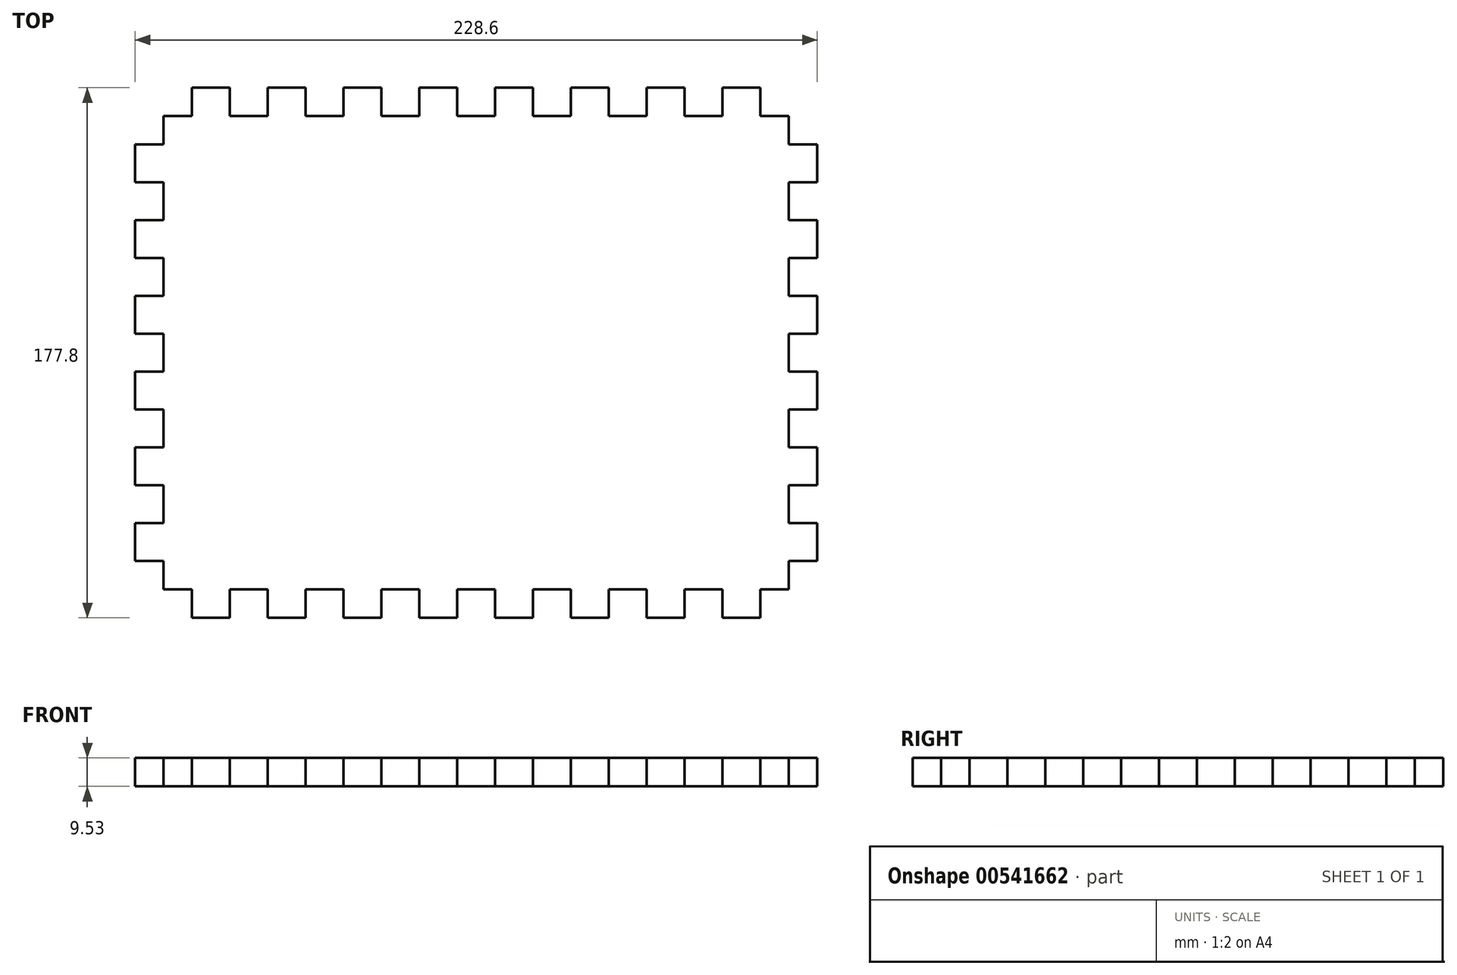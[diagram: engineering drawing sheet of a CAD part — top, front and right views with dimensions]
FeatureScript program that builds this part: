
annotation { "Feature Type Name" : "Feature", "Feature Type Description" : "" }
export const myFeature = defineFeature(function(context is Context, id is Id, definition is map)
    precondition{}
    {
        {
            var Q0;
            Q0=qCreatedBy(makeId("Top.planeOp"),FACE);
            var sketch = newSketch(context, id + "F0", { "sketchPlane" : qUnion([Q0])});
            skLineSegment(sketch, "E0.bottom", {"start": v(19.05, 0) * mm, "end": v(31.75, 0) * mm});
            skLineSegment(sketch, "E0.left", {"start": v(0, -19.05) * mm, "end": v(0, -31.75) * mm});
            skLineSegment(sketch, "E1", {"start": v(9.52, -9.53) * mm, "end": v(19.05, -9.53) * mm});
            skLineSegment(sketch, "E2", {"start": v(19.05, -9.53) * mm, "end": v(19.05, 0) * mm});
            skLineSegment(sketch, "E3", {"start": v(31.75, 0) * mm, "end": v(31.75, -9.53) * mm});
            skLineSegment(sketch, "E4", {"start": v(31.75, -9.53) * mm, "end": v(44.45, -9.53) * mm});
            skLineSegment(sketch, "E5", {"start": v(44.45, -9.53) * mm, "end": v(44.45, 0) * mm});
            skLineSegment(sketch, "E6", {"start": v(44.45, 0) * mm, "end": v(57.15, 0) * mm});
            skLineSegment(sketch, "E7", {"start": v(57.15, 0) * mm, "end": v(57.15, -9.53) * mm});
            skLineSegment(sketch, "E8", {"start": v(57.15, -9.53) * mm, "end": v(69.85, -9.53) * mm});
            skLineSegment(sketch, "E9", {"start": v(69.85, -9.53) * mm, "end": v(69.85, 0) * mm});
            skLineSegment(sketch, "E10", {"start": v(69.85, 0) * mm, "end": v(82.55, 0) * mm});
            skLineSegment(sketch, "E11", {"start": v(82.55, 0) * mm, "end": v(82.55, -9.53) * mm});
            skLineSegment(sketch, "E12", {"start": v(82.55, -9.53) * mm, "end": v(95.25, -9.53) * mm});
            skLineSegment(sketch, "E13", {"start": v(95.25, -9.53) * mm, "end": v(95.25, 0) * mm});
            skLineSegment(sketch, "E14", {"start": v(95.25, 0) * mm, "end": v(107.95, 0) * mm});
            skLineSegment(sketch, "E15", {"start": v(107.95, 0) * mm, "end": v(107.95, -9.53) * mm});
            skLineSegment(sketch, "E16", {"start": v(107.95, -9.53) * mm, "end": v(120.65, -9.53) * mm});
            skLineSegment(sketch, "E17", {"start": v(120.65, -9.53) * mm, "end": v(120.65, 0) * mm});
            skLineSegment(sketch, "E18.trimOffspring", {"start": v(120.65, 0) * mm, "end": v(133.35, 0) * mm});
            skLineSegment(sketch, "E19", {"start": v(9.52, -9.53) * mm, "end": v(9.52, -19.05) * mm});
            skLineSegment(sketch, "E20", {"start": v(9.52, -19.05) * mm, "end": v(0, -19.05) * mm});
            skPoint(sketch, "E21.orphan", {"position": v(0, 0) * mm});
            skLineSegment(sketch, "E22", {"start": v(133.35, 0) * mm, "end": v(133.35, -9.53) * mm});
            skLineSegment(sketch, "E23", {"start": v(133.35, -9.53) * mm, "end": v(146.05, -9.53) * mm});
            skLineSegment(sketch, "E24", {"start": v(146.05, -9.53) * mm, "end": v(146.05, 0) * mm});
            skLineSegment(sketch, "E25", {"start": v(146.05, 0) * mm, "end": v(158.75, 0) * mm});
            skLineSegment(sketch, "E26", {"start": v(158.75, 0) * mm, "end": v(158.75, -9.53) * mm});
            skLineSegment(sketch, "E27", {"start": v(158.75, -9.53) * mm, "end": v(171.45, -9.53) * mm});
            skLineSegment(sketch, "E28", {"start": v(171.45, -9.53) * mm, "end": v(171.45, 0) * mm});
            skLineSegment(sketch, "E29", {"start": v(171.45, 0) * mm, "end": v(184.15, 0) * mm});
            skLineSegment(sketch, "E30", {"start": v(184.15, 0) * mm, "end": v(184.15, -9.53) * mm});
            skLineSegment(sketch, "E31", {"start": v(184.15, -9.53) * mm, "end": v(196.85, -9.53) * mm});
            skLineSegment(sketch, "E32", {"start": v(196.85, -9.53) * mm, "end": v(196.85, 0) * mm});
            skLineSegment(sketch, "E33.trimOffspring", {"start": v(196.85, 0) * mm, "end": v(209.55, 0) * mm});
            skLineSegment(sketch, "E34", {"start": v(209.55, 0) * mm, "end": v(209.55, -9.53) * mm});
            skLineSegment(sketch, "E35", {"start": v(209.55, -9.53) * mm, "end": v(219.08, -9.53) * mm});
            skLineSegment(sketch, "E36", {"start": v(219.08, -9.53) * mm, "end": v(219.08, -19.05) * mm});
            skLineSegment(sketch, "E37", {"start": v(219.08, -19.05) * mm, "end": v(228.6, -19.05) * mm});
            skPoint(sketch, "E38.orphan", {"position": v(228.6, 0) * mm});
            skLineSegment(sketch, "E39", {"start": v(0, -31.75) * mm, "end": v(9.53, -31.75) * mm});
            skLineSegment(sketch, "E40", {"start": v(9.53, -31.75) * mm, "end": v(9.53, -44.45) * mm});
            skLineSegment(sketch, "E41", {"start": v(9.53, -44.45) * mm, "end": v(0, -44.45) * mm});
            skLineSegment(sketch, "E42", {"start": v(0, -44.45) * mm, "end": v(0, -57.15) * mm});
            skLineSegment(sketch, "E43", {"start": v(0, -57.15) * mm, "end": v(9.53, -57.15) * mm});
            skLineSegment(sketch, "E44", {"start": v(9.53, -57.15) * mm, "end": v(9.53, -69.85) * mm});
            skLineSegment(sketch, "E45", {"start": v(9.53, -69.85) * mm, "end": v(0, -69.85) * mm});
            skLineSegment(sketch, "E46", {"start": v(0, -69.85) * mm, "end": v(0, -82.55) * mm});
            skLineSegment(sketch, "E47", {"start": v(0, -82.55) * mm, "end": v(9.53, -82.55) * mm});
            skLineSegment(sketch, "E48", {"start": v(9.53, -82.55) * mm, "end": v(9.53, -95.25) * mm});
            skLineSegment(sketch, "E49", {"start": v(9.53, -95.25) * mm, "end": v(0, -95.25) * mm});
            skLineSegment(sketch, "E50", {"start": v(0, -95.25) * mm, "end": v(0, -107.95) * mm});
            skLineSegment(sketch, "E51", {"start": v(0, -107.95) * mm, "end": v(9.53, -107.95) * mm});
            skLineSegment(sketch, "E52", {"start": v(9.53, -107.95) * mm, "end": v(9.53, -120.65) * mm});
            skLineSegment(sketch, "E53", {"start": v(9.53, -120.65) * mm, "end": v(0, -120.65) * mm});
            skLineSegment(sketch, "E54.trimOffspring", {"start": v(0, -120.65) * mm, "end": v(0, -133.35) * mm});
            skLineSegment(sketch, "E55", {"start": v(0, -133.35) * mm, "end": v(9.53, -133.35) * mm});
            skLineSegment(sketch, "E56", {"start": v(9.53, -133.35) * mm, "end": v(9.53, -146.05) * mm});
            skLineSegment(sketch, "E57", {"start": v(9.53, -146.05) * mm, "end": v(0, -146.05) * mm});
            skLineSegment(sketch, "E58", {"start": v(0, -146.05) * mm, "end": v(0, -158.75) * mm});
            skLineSegment(sketch, "E59", {"start": v(0, -158.75) * mm, "end": v(9.53, -158.75) * mm});
            skLineSegment(sketch, "E60", {"start": v(9.53, -158.75) * mm, "end": v(9.53, -168.28) * mm});
            skPoint(sketch, "E61.orphan", {"position": v(0, -177.8) * mm});
            skLineSegment(sketch, "E62", {"start": v(114.3, -9.52) * mm, "end": v(114.3, -62.32) * mm, "construction": true});
            skLineSegment(sketch, "E63", {"start": v(9.53, -88.9) * mm, "end": v(69.46, -88.9) * mm, "construction": true});
            skPoint(sketch, "E63.endSnap0", {"position": v(9.53, -88.9) * mm});
            skLineSegment(sketch, "E64.MirrorCS", {"start": v(228.6, -19.05) * mm, "end": v(228.6, -31.75) * mm});
            skLineSegment(sketch, "E65.MirrorCS", {"start": v(228.6, -31.75) * mm, "end": v(219.08, -31.75) * mm});
            skLineSegment(sketch, "E66.MirrorCS", {"start": v(219.08, -31.75) * mm, "end": v(219.08, -44.45) * mm});
            skLineSegment(sketch, "E67.MirrorCS", {"start": v(219.08, -44.45) * mm, "end": v(228.6, -44.45) * mm});
            skLineSegment(sketch, "E68.MirrorCS", {"start": v(228.6, -44.45) * mm, "end": v(228.6, -57.15) * mm});
            skLineSegment(sketch, "E69.MirrorCS", {"start": v(228.6, -57.15) * mm, "end": v(219.08, -57.15) * mm});
            skLineSegment(sketch, "E70.MirrorCS", {"start": v(219.08, -57.15) * mm, "end": v(219.08, -69.85) * mm});
            skLineSegment(sketch, "E71.MirrorCS", {"start": v(219.08, -69.85) * mm, "end": v(228.6, -69.85) * mm});
            skLineSegment(sketch, "E72.MirrorCS", {"start": v(228.6, -69.85) * mm, "end": v(228.6, -82.55) * mm});
            skLineSegment(sketch, "E73.MirrorCS", {"start": v(228.6, -82.55) * mm, "end": v(219.08, -82.55) * mm});
            skLineSegment(sketch, "E74.MirrorCS", {"start": v(219.08, -82.55) * mm, "end": v(219.08, -95.25) * mm});
            skLineSegment(sketch, "E75.MirrorCS", {"start": v(219.08, -95.25) * mm, "end": v(228.6, -95.25) * mm});
            skLineSegment(sketch, "E76.MirrorCS", {"start": v(228.6, -95.25) * mm, "end": v(228.6, -107.95) * mm});
            skLineSegment(sketch, "E77.MirrorCS", {"start": v(228.6, -107.95) * mm, "end": v(219.08, -107.95) * mm});
            skLineSegment(sketch, "E78.MirrorCS", {"start": v(219.08, -107.95) * mm, "end": v(219.08, -120.65) * mm});
            skLineSegment(sketch, "E79.MirrorCS", {"start": v(219.08, -120.65) * mm, "end": v(228.6, -120.65) * mm});
            skLineSegment(sketch, "E80.MirrorCS", {"start": v(228.6, -120.65) * mm, "end": v(228.6, -133.35) * mm});
            skLineSegment(sketch, "E81.MirrorCS", {"start": v(228.6, -133.35) * mm, "end": v(219.08, -133.35) * mm});
            skLineSegment(sketch, "E82.MirrorCS", {"start": v(219.08, -133.35) * mm, "end": v(219.08, -146.05) * mm});
            skLineSegment(sketch, "E83.MirrorCS", {"start": v(219.08, -146.05) * mm, "end": v(228.6, -146.05) * mm});
            skLineSegment(sketch, "E84.MirrorCS", {"start": v(228.6, -146.05) * mm, "end": v(228.6, -158.75) * mm});
            skLineSegment(sketch, "E85.MirrorCS", {"start": v(228.6, -158.75) * mm, "end": v(219.08, -158.75) * mm});
            skLineSegment(sketch, "E86.MirrorCS", {"start": v(219.08, -158.75) * mm, "end": v(219.08, -171.11) * mm});
            skLineSegment(sketch, "E87.MirrorCS", {"start": v(9.52, -168.28) * mm, "end": v(19.05, -168.28) * mm});
            skLineSegment(sketch, "E88.MirrorCS", {"start": v(19.05, -168.28) * mm, "end": v(19.05, -177.8) * mm});
            skLineSegment(sketch, "E89.MirrorCS", {"start": v(19.05, -177.8) * mm, "end": v(31.75, -177.8) * mm});
            skLineSegment(sketch, "E90.MirrorCS", {"start": v(31.75, -177.8) * mm, "end": v(31.75, -168.28) * mm});
            skLineSegment(sketch, "E91.MirrorCS", {"start": v(31.75, -168.28) * mm, "end": v(44.45, -168.28) * mm});
            skLineSegment(sketch, "E92.MirrorCS", {"start": v(44.45, -168.28) * mm, "end": v(44.45, -177.8) * mm});
            skLineSegment(sketch, "E93.MirrorCS", {"start": v(44.45, -177.8) * mm, "end": v(57.15, -177.8) * mm});
            skLineSegment(sketch, "E94.MirrorCS", {"start": v(57.15, -168.28) * mm, "end": v(69.85, -168.28) * mm});
            skLineSegment(sketch, "E95.MirrorCS", {"start": v(69.85, -168.28) * mm, "end": v(69.85, -177.8) * mm});
            skLineSegment(sketch, "E96.MirrorCS", {"start": v(69.85, -177.8) * mm, "end": v(82.55, -177.8) * mm});
            skLineSegment(sketch, "E97.MirrorCS", {"start": v(82.55, -177.8) * mm, "end": v(82.55, -168.28) * mm});
            skLineSegment(sketch, "E98.MirrorCS", {"start": v(82.55, -168.28) * mm, "end": v(95.25, -168.28) * mm});
            skLineSegment(sketch, "E99.MirrorCS", {"start": v(95.25, -168.28) * mm, "end": v(95.25, -177.8) * mm});
            skLineSegment(sketch, "E100.MirrorCS", {"start": v(95.25, -177.8) * mm, "end": v(107.95, -177.8) * mm});
            skLineSegment(sketch, "E101.MirrorCS", {"start": v(57.15, -177.8) * mm, "end": v(57.15, -168.28) * mm});
            skLineSegment(sketch, "E102.MirrorCS", {"start": v(107.95, -168.28) * mm, "end": v(120.65, -168.28) * mm});
            skLineSegment(sketch, "E103.MirrorCS", {"start": v(120.65, -168.28) * mm, "end": v(120.65, -177.8) * mm});
            skLineSegment(sketch, "E104.MirrorCS", {"start": v(120.65, -177.8) * mm, "end": v(133.35, -177.8) * mm});
            skLineSegment(sketch, "E105.MirrorCS", {"start": v(133.35, -177.8) * mm, "end": v(133.35, -168.28) * mm});
            skLineSegment(sketch, "E106.MirrorCS", {"start": v(146.05, -168.28) * mm, "end": v(146.05, -177.8) * mm});
            skLineSegment(sketch, "E107.MirrorCS", {"start": v(146.05, -177.8) * mm, "end": v(158.75, -177.8) * mm});
            skLineSegment(sketch, "E108.MirrorCS", {"start": v(158.75, -177.8) * mm, "end": v(158.75, -168.28) * mm});
            skLineSegment(sketch, "E109.MirrorCS", {"start": v(158.75, -168.28) * mm, "end": v(171.45, -168.28) * mm});
            skLineSegment(sketch, "E110.MirrorCS", {"start": v(171.45, -168.28) * mm, "end": v(171.45, -177.8) * mm});
            skLineSegment(sketch, "E111.MirrorCS", {"start": v(171.45, -177.8) * mm, "end": v(184.15, -177.8) * mm});
            skLineSegment(sketch, "E112.MirrorCS", {"start": v(184.15, -177.8) * mm, "end": v(184.15, -168.28) * mm});
            skLineSegment(sketch, "E113.MirrorCS", {"start": v(184.15, -168.28) * mm, "end": v(196.85, -168.28) * mm});
            skLineSegment(sketch, "E114.MirrorCS", {"start": v(196.85, -168.28) * mm, "end": v(196.85, -177.8) * mm});
            skLineSegment(sketch, "E115.MirrorCS", {"start": v(196.85, -177.8) * mm, "end": v(209.55, -177.8) * mm});
            skLineSegment(sketch, "E116.MirrorCS", {"start": v(209.55, -177.8) * mm, "end": v(209.55, -168.28) * mm});
            skLineSegment(sketch, "E117.MirrorCS", {"start": v(209.55, -168.28) * mm, "end": v(219.08, -168.28) * mm});
            skLineSegment(sketch, "E118.MirrorCS", {"start": v(107.95, -177.8) * mm, "end": v(107.95, -168.28) * mm});
            skLineSegment(sketch, "E119.MirrorCS", {"start": v(133.35, -168.28) * mm, "end": v(146.05, -168.28) * mm});
            skSolve(sketch);
        }
        {
            var Q0;
            Q0=makeQuery(id+"F0.imprint","IMPRINT",FACE,{"disambiguationData":[TD([[makeQuery(id+"F0.imprint","IMPRINT",EDGE,{"derivedFrom":sQuery(id+"F0.wireOp",EDGE,"E1")}),-1.0]])]});
            extrude(context, id + "F1", {"entities" : qUnion([Q0]), "depth" : 9.52 * mm, "offsetDistance" : 25.4 * mm});
        }
    });
